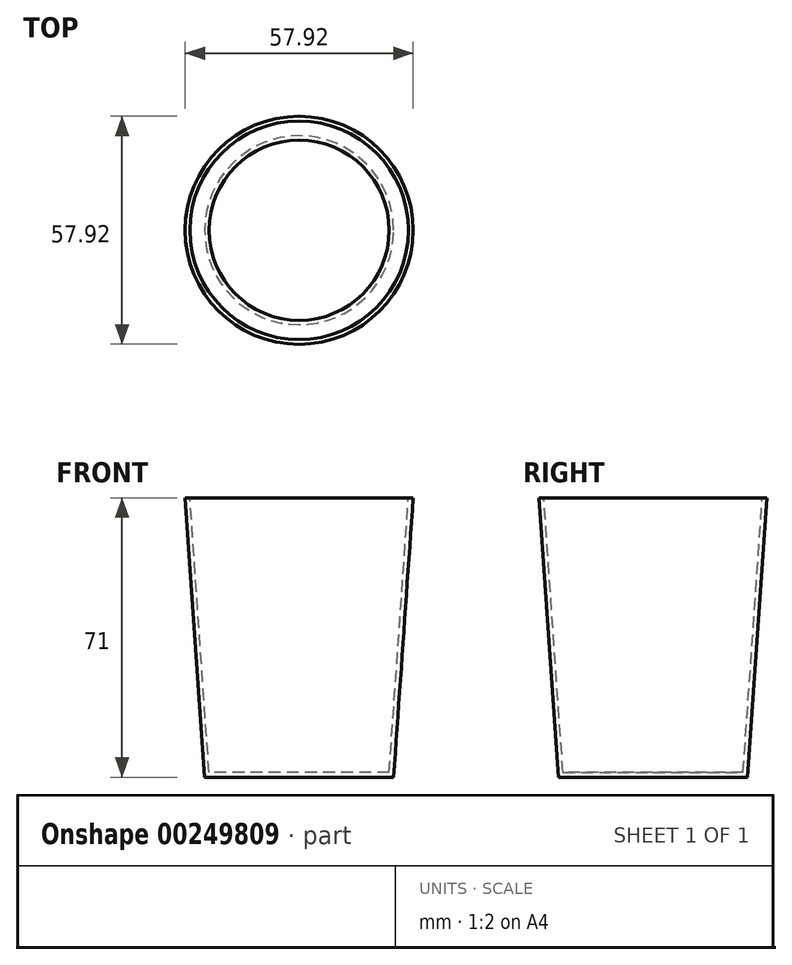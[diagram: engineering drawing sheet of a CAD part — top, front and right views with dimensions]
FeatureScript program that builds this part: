
annotation { "Feature Type Name" : "Feature", "Feature Type Description" : "" }
export const myFeature = defineFeature(function(context is Context, id is Id, definition is map)
    precondition{}
    {
        {
            var Q0;
            Q0=qCreatedBy(makeId("Top.planeOp"),FACE);
            var sketch = newSketch(context, id + "F0", { "sketchPlane" : qUnion([Q0])});
            skCircle(sketch, "E0", {"center": v(0, 0) * mm, "radius": 24 * mm});
            skSolve(sketch);
        }
        {
            var Q0;
            Q0 = qSketchRegion(id + "F0", true);
            extrude(context, id + "F1", {"entities" : qUnion([Q0]), "depth" : 71 * mm, "hasDraft" : true, "draftAngle" : 4 * degree});
        }
        {
            var Q0;
            Q0=makeQuery(id+"F1.opExtrude","CAP_FACE",FACE,{"disambiguationData":[OSD([sQuery(id+"F0.wireOp",EDGE,"E0")])],"isStart":false});
            shell(context, id + "F2", {"entities" : qUnion([Q0]), "thickness" : 1.2 * mm});
        }
    });
